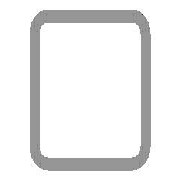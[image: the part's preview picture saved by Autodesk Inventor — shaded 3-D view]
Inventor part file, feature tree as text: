
AUTODESK INVENTOR PART (.ipt)
format: ipt  version: 2025.3 (Build 293356000, 356)  size: 134,144 bytes
history: native  units: mm (DEFAULTED — no unit token found)
features: other x4, sketch x1, plane x1
ambient origin geometry x8: Origin, YZ Plane, XZ Plane, XY Plane, X Axis, Y Axis, Z Axis, Center Point
bodies: Solid1 (feature_tree), Body (feature_tree)
feature tree (6):
  parser-record x1  (decoder bookkeeping rows leaked as tree rows — omitted from the tree; the rows remain in map.json)
  other  "Driven Length"
  other  "Start Plane"
  other  "End Plane"
  sketch  "Sketch3"  dims[d3=2040.0mm d4=0.0mm d7=6.0mm d9=80.0mm d11=80.0mm d12=3.0mm d13=80.0mm d14=2120.0mm d15=40.0mm d16=40.0mm d17=90.0deg d18=2040.0mm]
  plane  "Work Plane3"
